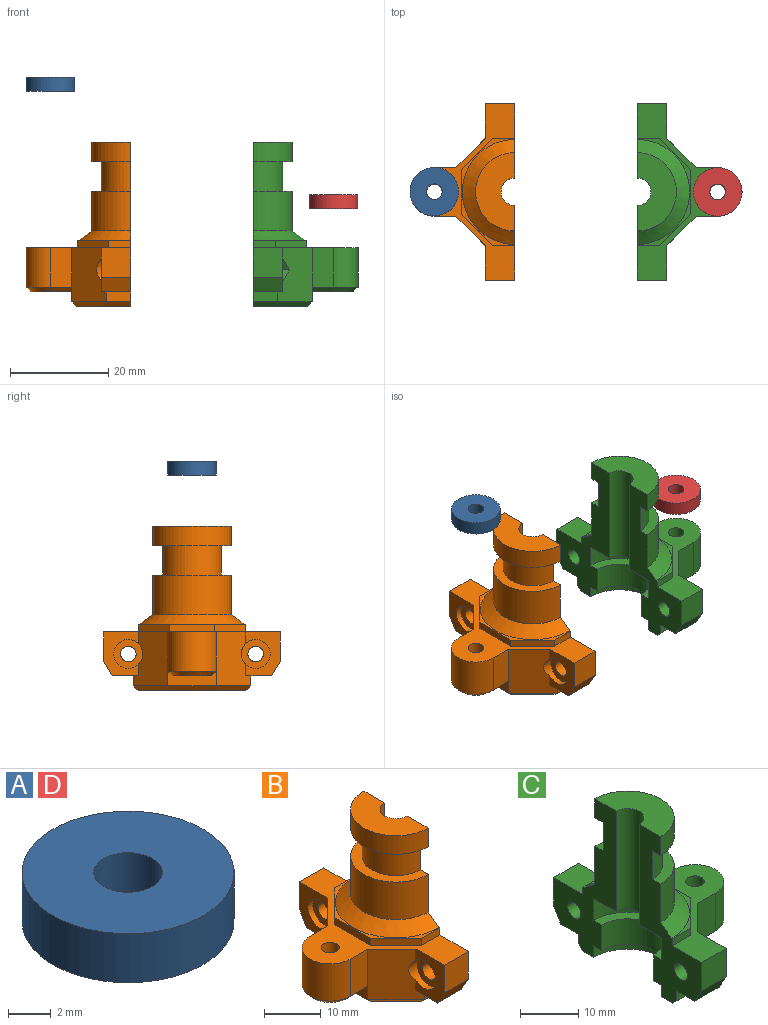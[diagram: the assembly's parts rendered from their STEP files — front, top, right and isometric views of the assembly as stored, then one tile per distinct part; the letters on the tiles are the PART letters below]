
ASSEMBLY  parts=4 mates=3
PART A: 4 faces, bbox 9.9x9.9x2.8 mm
  f0: plane 9.9x9.9mm, normal (0,0,1), area 68.9mm2, adj f2,f3
  f1: plane 9.9x9.9mm, normal (0,0,-1), area 68.9mm2, adj f2,f3
  f2: cylinder r=4.95mm len=9.9mm, axis (0,0,-1), area 87.1mm2, adj f0,f1
  f3: cylinder r=1.6mm len=3.2mm, axis (0,0,-1), area 28.1mm2, adj f0,f1
PART B: 58 faces, bbox 21.4x36x33.6 mm
  f0: plane 9x7.03mm, normal (-1,0,0), area 36mm2, adj f12,f13,f15,f19,f32,f49
  f1: plane 6x5.33mm, normal (0,0,-1), area 26.3mm2, adj f16,f20,f36,f37,f40
  f2: cylinder r=8mm len=16mm, axis (0,0,-1), area 203.6mm2, adj f8,f11,f39,f40
  f3: plane 4.52x1.5mm, normal (0,1,0), area 6.8mm2, adj f5,f12,f29,f40
  f4: plane 4.52x1.5mm, normal (0,-1,0), area 6.8mm2, adj f5,f12,f31,f39
  f5: plane 21.8x10.9mm, normal (0,0,1), area 17mm2, adj f3,f4,f11,f29,f30,f31,f39,f40
  f6: cylinder r=6mm len=12mm, axis (0,0,-1), area 113.1mm2, adj f7,f8,f39,f40
  f7: plane 16x8mm, normal (0,0,-1), area 44mm2, adj f6,f10,f39,f40
  f8: plane 16x8mm, normal (0,0,1), area 44mm2, adj f2,f6,f39,f40
  f9: plane 16x8mm, normal (0,0,1), area 88.2mm2, adj f10,f27,f39,f40
  f10: cylinder r=8mm len=16mm, axis (0,0,-1), area 100.5mm2, adj f7,f9,f39,f40
  f11: cone r=8mm half-angle=53.5deg, axis (0,0,-1), area 98.7mm2, adj f2,f5,f39,f40
  f12: plane 36x21.37mm, normal (0,0,1), area 189.3mm2, adj f0,f3,f4,f13,f14,f29,f30,f31
  f13: plane 6x6mm, normal (0,-1,0), area 36mm2, adj f0,f12,f19,f39
  f14: plane 6.06x6mm, normal (0,1,0), area 36.3mm2, adj f12,f20,f37,f40
  f15: plane 6x5.3mm, normal (0,0,-1), area 26.1mm2, adj f0,f18,f19,f32,f39
  f16: plane 4.97x2mm, normal (0,1,0), area 9.9mm2, adj f1,f36,f40,f57
  f17: plane 22x11mm, normal (0,0,-1), area 92.3mm2, adj f21,f39,f40,f53,f54,f55,f56,f57
  f18: plane 4.97x2mm, normal (0,-1,0), area 9.9mm2, adj f15,f32,f39,f53
  f19: plane 6x3mm, normal (0,-0.87,-0.5), area 20.8mm2, adj f0,f13,f15,f39
  f20: plane 6x2.94mm, normal (0,0.87,-0.5), area 20.4mm2, adj f1,f14,f37,f40
  f21: cylinder r=8.3mm len=16.6mm, axis (0,0,-1), area 62.6mm2, adj f17,f25,f39,f40
  f22: plane 16.6x8.3mm, normal (0,0,-1), area 95.9mm2, adj f26,f27,f39,f40
  f23: cylinder r=6.3mm len=12.6mm, axis (0,0,-1), area 106.9mm2, adj f24,f25,f39,f40
  f24: plane 16.6x8.3mm, normal (0,0,1), area 45.9mm2, adj f23,f26,f39,f40
  f25: plane 16.6x8.3mm, normal (0,0,-1), area 45.9mm2, adj f21,f23,f39,f40
  f26: cylinder r=8.3mm len=16.6mm, axis (0,0,-1), area 119.9mm2, adj f22,f24,f39,f40
  f27: cylinder r=2.8mm len=21.2mm, axis (0,0,1), area 186.5mm2, adj f9,f22,f39,f40
  f28: plane 8.37x7.94mm, normal (0,0,-1), area 32.4mm2, adj f38,f43,f50,f51,f52
  f29: plane 6.39x6.39mm, normal (-0.71,0.71,0), area 13.5mm2, adj f3,f5,f12,f30
  f30: plane 9.03x1.5mm, normal (-1,0,0), area 13.5mm2, adj f5,f12,f29,f31
  f31: plane 6.39x6.39mm, normal (-0.71,-0.71,0), area 13.5mm2, adj f4,f5,f12,f30
  f32: plane 11x7.03mm, normal (-0.71,-0.71,0), area 92.4mm2, adj f0,f12,f15,f18,f33,f38,f49,f54
  f33: plane 8x4.4mm, normal (0,-1,0), area 35.2mm2, adj f12,f32,f34,f52
  f34: cylinder r=4.97mm len=9.94mm, axis (0,0,1), area 124.9mm2, adj f12,f33,f35,f51
  f35: plane 8x4.4mm, normal (0,1,0), area 35.2mm2, adj f12,f34,f36,f50
  f36: plane 11x7.03mm, normal (-0.71,0.71,0), area 92.4mm2, adj f1,f12,f16,f35,f37,f38,f46,f56
  f37: plane 9x7.03mm, normal (-1,0,0), area 36.1mm2, adj f1,f12,f14,f20,f36,f46
  f38: plane 9.94x3mm, normal (-1,0,0), area 20.9mm2, adj f28,f32,f36,f50,f52,f55
  f39: plane 33.6x15.2mm, normal (1,0,0), area 203.2mm2, adj f2,f4,f5,f6,f7,f8,f9,f10
  f40: plane 33.6x15.2mm, normal (1,0,0), area 203.3mm2, adj f1,f2,f3,f5,f6,f7,f8,f9
  f41: cylinder r=1.6mm len=7.8mm, axis (0,0,-1), area 78.4mm2, adj f12,f42
  f42: plane 5.9x5.9mm, normal (0,0,-1), area 19.3mm2, adj f41,f43
  f43: cylinder r=2.95mm len=5.9mm, axis (0,0,-1), area 22.2mm2, adj f28,f42
  f44: cylinder r=1.6mm len=4.8mm, axis (-1,0,0), area 48.3mm2, adj f40,f45
  f45: plane 5.9x5.9mm, normal (-1,0,0), area 19.3mm2, adj f44,f46
  f46: cylinder r=2.95mm len=5.9mm, axis (-1,0,0), area 25.2mm2, adj f36,f37,f45
  f47: cylinder r=1.6mm len=4.8mm, axis (-1,0,0), area 48.3mm2, adj f39,f48
  f48: plane 5.9x5.9mm, normal (-1,0,0), area 19.3mm2, adj f47,f49
  f49: cylinder r=2.95mm len=5.9mm, axis (-1,0,0), area 25.2mm2, adj f0,f32,f48
  f50: plane 4.4x1mm, normal (0,0.71,-0.71), area 6.2mm2, adj f28,f35,f38,f51
  f51: cone r=3.97mm half-angle=45deg, axis (0,0,1), area 19.9mm2, adj f28,f34,f50,f52
  f52: plane 4.4x1mm, normal (0,-0.71,-0.71), area 6.2mm2, adj f28,f33,f38,f51
  f53: plane 4.97x1mm, normal (0,-0.71,-0.71), area 6.7mm2, adj f17,f18,f39,f54
  f54: plane 7.44x7.44mm, normal (-0.5,-0.5,-0.71), area 13.5mm2, adj f17,f32,f53,f55
  f55: plane 9.94x1mm, normal (-0.71,0,-0.71), area 13.5mm2, adj f17,f38,f54,f56
  f56: plane 7.44x7.44mm, normal (-0.5,0.5,-0.71), area 13.5mm2, adj f17,f36,f55,f57
  f57: plane 4.97x1mm, normal (0,0.71,-0.71), area 6.7mm2, adj f16,f17,f40,f56
PART C: 68 faces, bbox 21.4x36x33.6 mm
  f0: plane 11x7.03mm, normal (0.71,-0.71,0), area 91.6mm2, adj f1,f10,f11,f27,f30,f32,f48,f49
  f1: plane 9x7.03mm, normal (1,0,0), area 33.8mm2, adj f0,f19,f30,f31,f32,f47,f48,f49
  f2: cylinder r=1.6mm len=4mm, axis (-1,0,0), area 40.2mm2, adj f42,f53
  f3: cylinder r=1.6mm len=4mm, axis (-1,0,0), area 40.2mm2, adj f41,f46
  f4: plane 8.37x7.94mm, normal (0,0,-1), area 32.4mm2, adj f11,f45,f60,f61,f62
  f5: plane 6.39x6.39mm, normal (0.71,-0.71,0), area 13.5mm2, adj f6,f15,f32,f37
  f6: plane 9.03x1.5mm, normal (1,0,0), area 13.5mm2, adj f5,f7,f15,f32
  f7: plane 6.39x6.39mm, normal (0.71,0.71,0), area 13.5mm2, adj f6,f15,f32,f38
  f8: plane 8x4.4mm, normal (0,1,0), area 35.2mm2, adj f9,f12,f32,f60
  f9: cylinder r=4.97mm len=9.94mm, axis (0,0,1), area 124.9mm2, adj f8,f10,f32,f61
  f10: plane 8x4.4mm, normal (0,-1,0), area 35.2mm2, adj f0,f9,f32,f62
  f11: plane 9.94x3mm, normal (1,0,0), area 20.9mm2, adj f0,f4,f12,f60,f62,f65
  f12: plane 11x7.03mm, normal (0.71,0.71,0), area 91.6mm2, adj f8,f11,f13,f29,f32,f40,f54,f59
  f13: plane 9x7.03mm, normal (1,0,0), area 33.9mm2, adj f12,f17,f18,f32,f40,f54,f55,f56
  f14: cone r=8mm half-angle=53.5deg, axis (0,0,-1), area 98.7mm2, adj f15,f39,f41,f42
  f15: plane 21.8x10.9mm, normal (0,0,1), area 17mm2, adj f5,f6,f7,f14,f37,f38,f41,f42
  f16: plane 16x8mm, normal (0,0,1), area 44mm2, adj f36,f39,f41,f42
  f17: plane 6x2.94mm, normal (0,0.87,-0.5), area 20.4mm2, adj f13,f18,f40,f42
  f18: plane 6.06x6mm, normal (0,1,0), area 36.3mm2, adj f13,f17,f32,f42
  f19: plane 6x3mm, normal (0,-0.87,-0.5), area 20.8mm2, adj f1,f30,f31,f41
  f20: cylinder r=2.8mm len=21.2mm, axis (0,0,1), area 186.5mm2, adj f25,f34,f41,f42
  f21: plane 16.6x8.3mm, normal (0,0,-1), area 45.9mm2, adj f24,f26,f41,f42
  f22: cylinder r=8.3mm len=16.6mm, axis (0,0,-1), area 119.9mm2, adj f23,f25,f41,f42
  f23: plane 16.6x8.3mm, normal (0,0,1), area 45.9mm2, adj f22,f24,f41,f42
  f24: cylinder r=6.3mm len=12.6mm, axis (0,0,-1), area 106.9mm2, adj f21,f23,f41,f42
  f25: plane 16.6x8.3mm, normal (0,0,-1), area 95.9mm2, adj f20,f22,f41,f42
  f26: cylinder r=8.3mm len=16.6mm, axis (0,0,-1), area 62.6mm2, adj f21,f28,f41,f42
  f27: plane 4.97x2mm, normal (0,-1,0), area 9.9mm2, adj f0,f30,f41,f63
  f28: plane 22x11mm, normal (0,0,-1), area 92.3mm2, adj f26,f41,f42,f63,f64,f65,f66,f67
  f29: plane 4.97x2mm, normal (0,1,0), area 9.9mm2, adj f12,f40,f42,f67
  f30: plane 6x5.3mm, normal (0,0,-1), area 26.1mm2, adj f0,f1,f19,f27,f41
  f31: plane 6x6mm, normal (0,-1,0), area 36mm2, adj f1,f19,f32,f41
  f32: plane 36x21.37mm, normal (0,0,1), area 189.3mm2, adj f0,f1,f5,f6,f7,f8,f9,f10
  f33: cylinder r=8mm len=16mm, axis (0,0,-1), area 100.5mm2, adj f34,f35,f41,f42
  f34: plane 16x8mm, normal (0,0,1), area 88.2mm2, adj f20,f33,f41,f42
  f35: plane 16x8mm, normal (0,0,-1), area 44mm2, adj f33,f36,f41,f42
  f36: cylinder r=6mm len=12mm, axis (0,0,-1), area 113.1mm2, adj f16,f35,f41,f42
  f37: plane 4.52x1.5mm, normal (0,-1,0), area 6.8mm2, adj f5,f15,f32,f41
  f38: plane 4.52x1.5mm, normal (0,1,0), area 6.8mm2, adj f7,f15,f32,f42
  f39: cylinder r=8mm len=16mm, axis (0,0,-1), area 203.6mm2, adj f14,f16,f41,f42
  f40: plane 6x5.33mm, normal (0,0,-1), area 26.3mm2, adj f12,f13,f17,f29,f42
  f41: plane 33.6x15.2mm, normal (-1,0,0), area 203.2mm2, adj f3,f14,f15,f16,f19,f20,f21,f22
  f42: plane 33.6x15.2mm, normal (-1,0,0), area 203.3mm2, adj f2,f14,f15,f16,f17,f18,f20,f21
  f43: cylinder r=1.6mm len=7.8mm, axis (0,0,-1), area 78.4mm2, adj f32,f44
  f44: plane 5.9x5.9mm, normal (0,0,-1), area 19.3mm2, adj f43,f45
  f45: cylinder r=2.95mm len=5.9mm, axis (0,0,-1), area 22.2mm2, adj f4,f44
  f46: plane 6.81x5.9mm, normal (1,0,0), area 22.1mm2, adj f3,f47,f48,f49,f50,f51,f52
  f47: plane 3.41x2mm, normal (0,0,-1), area 6.8mm2, adj f1,f46,f48,f51
  f48: plane 3.38x2.95mm, normal (0,-0.87,-0.5), area 8.7mm2, adj f0,f1,f46,f47,f49
  f49: plane 3.38x2.95mm, normal (0,-0.87,0.5), area 8.7mm2, adj f0,f1,f46,f48,f50
  f50: plane 3.41x2mm, normal (0,0,1), area 6.8mm2, adj f1,f46,f49,f52
  f51: plane 2.95x2mm, normal (0,0.87,-0.5), area 6.8mm2, adj f1,f46,f47,f52
  f52: plane 2.95x2mm, normal (0,0.87,0.5), area 6.8mm2, adj f1,f46,f50,f51
  f53: plane 6.81x5.9mm, normal (1,0,0), area 22.1mm2, adj f2,f54,f55,f56,f57,f58,f59
  f54: plane 3.38x2.95mm, normal (0,0.87,-0.5), area 8.7mm2, adj f12,f13,f53,f55,f59
  f55: plane 3.41x2mm, normal (0,0,-1), area 6.8mm2, adj f13,f53,f54,f56
  f56: plane 2.95x2mm, normal (0,-0.87,-0.5), area 6.8mm2, adj f13,f53,f55,f57
  f57: plane 2.95x2mm, normal (0,-0.87,0.5), area 6.8mm2, adj f13,f53,f56,f58
  f58: plane 3.41x2mm, normal (0,0,1), area 6.8mm2, adj f13,f53,f57,f59
  f59: plane 3.38x2.95mm, normal (0,0.87,0.5), area 8.7mm2, adj f12,f13,f53,f54,f58
  f60: plane 4.4x1mm, normal (0,0.71,-0.71), area 6.2mm2, adj f4,f8,f11,f61
  f61: cone r=4.97mm half-angle=45deg, axis (0,0,1), area 19.9mm2, adj f4,f9,f60,f62
  f62: plane 4.4x1mm, normal (0,-0.71,-0.71), area 6.2mm2, adj f4,f10,f11,f61
  f63: plane 4.97x1mm, normal (0,-0.71,-0.71), area 6.7mm2, adj f27,f28,f41,f64
  f64: plane 7.44x7.44mm, normal (0.5,-0.5,-0.71), area 13.5mm2, adj f0,f28,f63,f65
  f65: plane 9.94x1mm, normal (0.71,0,-0.71), area 13.5mm2, adj f11,f28,f64,f66
  f66: plane 7.44x7.44mm, normal (0.5,0.5,-0.71), area 13.5mm2, adj f12,f28,f65,f67
  f67: plane 4.97x1mm, normal (0,0.71,-0.71), area 6.7mm2, adj f28,f29,f42,f66
PART D: same geometry as A
PLACE A rot(axis=(-1,0,0),180deg) t=(44,77.22,24.8)mm
PLACE B t=(44,1.22,0)mm
PLACE C t=(69,1.22,0)mm
PLACE D rot(axis=(-1,0,0),180deg) t=(101.8,77.22,0.8)mm
MATE fastened C.f2 <-> B.f44  axis (-1,0,0) through (37,52.22,-9.5)mm
MATE fastened D.f2 <-> C.f9  axis (0,0,-1) through (53.4,39.22,3)mm
MATE fastened A.f2 <-> B.f34  axis (0,0,-1) through (-4.4,39.22,27)mm
